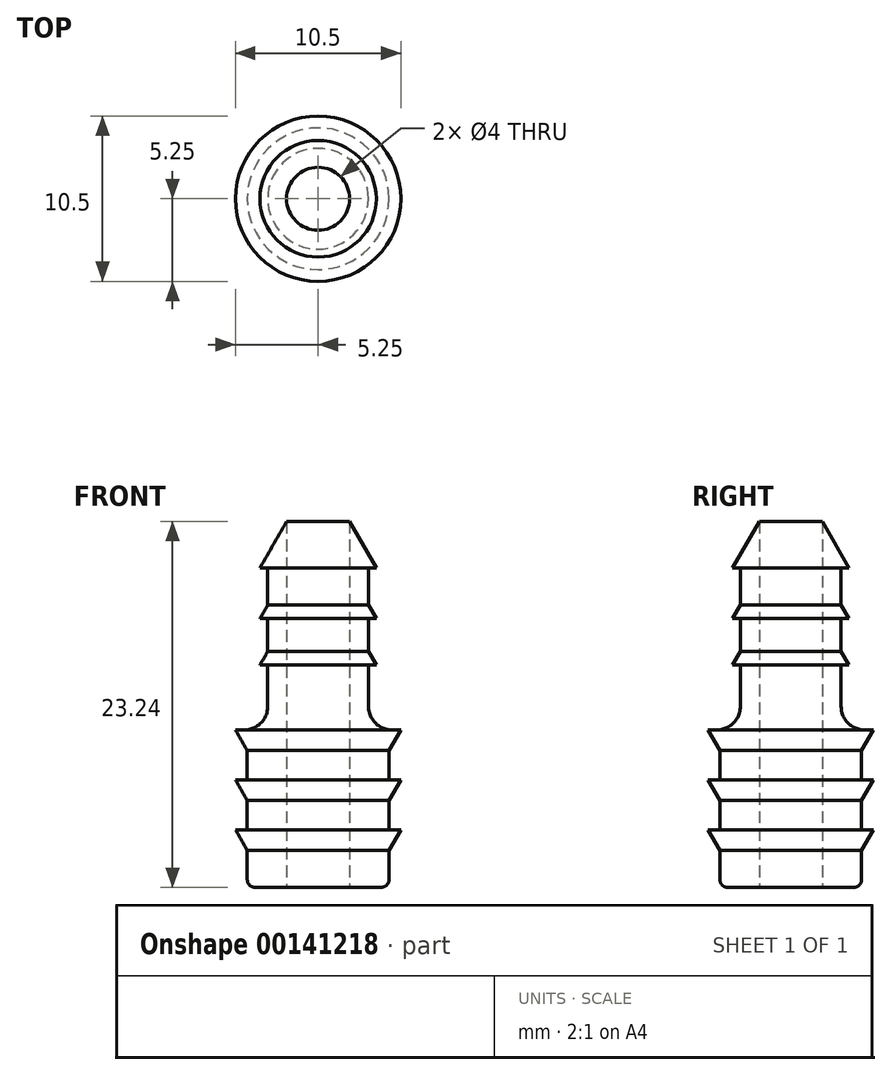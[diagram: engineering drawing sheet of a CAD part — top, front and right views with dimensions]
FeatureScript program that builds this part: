
annotation { "Feature Type Name" : "Feature", "Feature Type Description" : "" }
export const myFeature = defineFeature(function(context is Context, id is Id, definition is map)
    precondition{}
    {
        {
            var Q0;
            Q0=qCreatedBy(makeId("Front.planeOp"),FACE);
            var sketch = newSketch(context, id + "F0", { "sketchPlane" : qUnion([Q0])});
            skLineSegment(sketch, "E0", {"start": v(-2, 9.28) * mm, "end": v(-2, 32.52) * mm});
            skLineSegment(sketch, "E1", {"start": v(-2, 32.52) * mm, "end": v(-3.7, 29.58) * mm});
            skLineSegment(sketch, "E2", {"start": v(-3.7, 29.58) * mm, "end": v(-3.2, 29.58) * mm});
            skLineSegment(sketch, "E3", {"start": v(-3.2, 29.58) * mm, "end": v(-3.2, 27.21) * mm});
            skLineSegment(sketch, "E4", {"start": v(-3.2, 27.21) * mm, "end": v(-3.7, 26.35) * mm});
            skLineSegment(sketch, "E5", {"start": v(-3.7, 26.35) * mm, "end": v(-3.2, 26.35) * mm});
            skLineSegment(sketch, "E6", {"start": v(-3.2, 26.35) * mm, "end": v(-3.2, 24.26) * mm});
            skLineSegment(sketch, "E7", {"start": v(-3.2, 24.26) * mm, "end": v(-3.7, 23.4) * mm});
            skLineSegment(sketch, "E8", {"start": v(-3.7, 23.4) * mm, "end": v(-3.2, 23.4) * mm});
            skLineSegment(sketch, "E9", {"start": v(-3.2, 23.4) * mm, "end": v(-3.2, 20.78) * mm});
            skLineSegment(sketch, "E10", {"start": v(-4.7, 19.28) * mm, "end": v(-5.25, 19.28) * mm});
            skLineSegment(sketch, "E11", {"start": v(-5.25, 19.28) * mm, "end": v(-4.5, 17.98) * mm});
            skLineSegment(sketch, "E12", {"start": v(-4.5, 17.98) * mm, "end": v(-4.5, 16.11) * mm});
            skLineSegment(sketch, "E13", {"start": v(-4.5, 16.11) * mm, "end": v(-5.25, 16.11) * mm});
            skLineSegment(sketch, "E14", {"start": v(-5.25, 16.11) * mm, "end": v(-4.5, 14.81) * mm});
            skLineSegment(sketch, "E15", {"start": v(-4.5, 14.81) * mm, "end": v(-4.5, 12.95) * mm});
            skLineSegment(sketch, "E16", {"start": v(-4.5, 12.95) * mm, "end": v(-5.25, 12.95) * mm});
            skLineSegment(sketch, "E17", {"start": v(-5.25, 12.95) * mm, "end": v(-4.5, 11.65) * mm});
            skPoint(sketch, "E18.visualSharp", {"position": v(-3.2, 19.28) * mm});
            skArc(sketch, "E18.filletArc", {"start": v(-4.7, 19.28) * mm, "mid": v(-3.64, 19.72) * mm, "end": v(-3.2, 20.78) * mm});
            skLineSegment(sketch, "E19", {"start": v(0, 0) * mm, "end": v(0, 26.19) * mm, "construction": true});
            skLineSegment(sketch, "E20", {"start": v(-4.5, 11.65) * mm, "end": v(-4.5, 9.78) * mm});
            skLineSegment(sketch, "E21", {"start": v(-4, 9.28) * mm, "end": v(-2, 9.28) * mm});
            skArc(sketch, "E22.filletArc", {"start": v(-4.5, 9.78) * mm, "mid": v(-4.35, 9.43) * mm, "end": v(-4, 9.28) * mm});
            skSolve(sketch);
        }
        {
            var Q0;
            Q0 = qSketchRegion(id + "F0", true);
            var Q1;
            Q1=sQuery(id+"F0.wireOp",EDGE,"E19");
            revolve(context, id + "F1", {"entities" : qUnion([Q0]), "axis" : qUnion([Q1]), "revolveType" : RevolveType.FULL});
        }
    });
